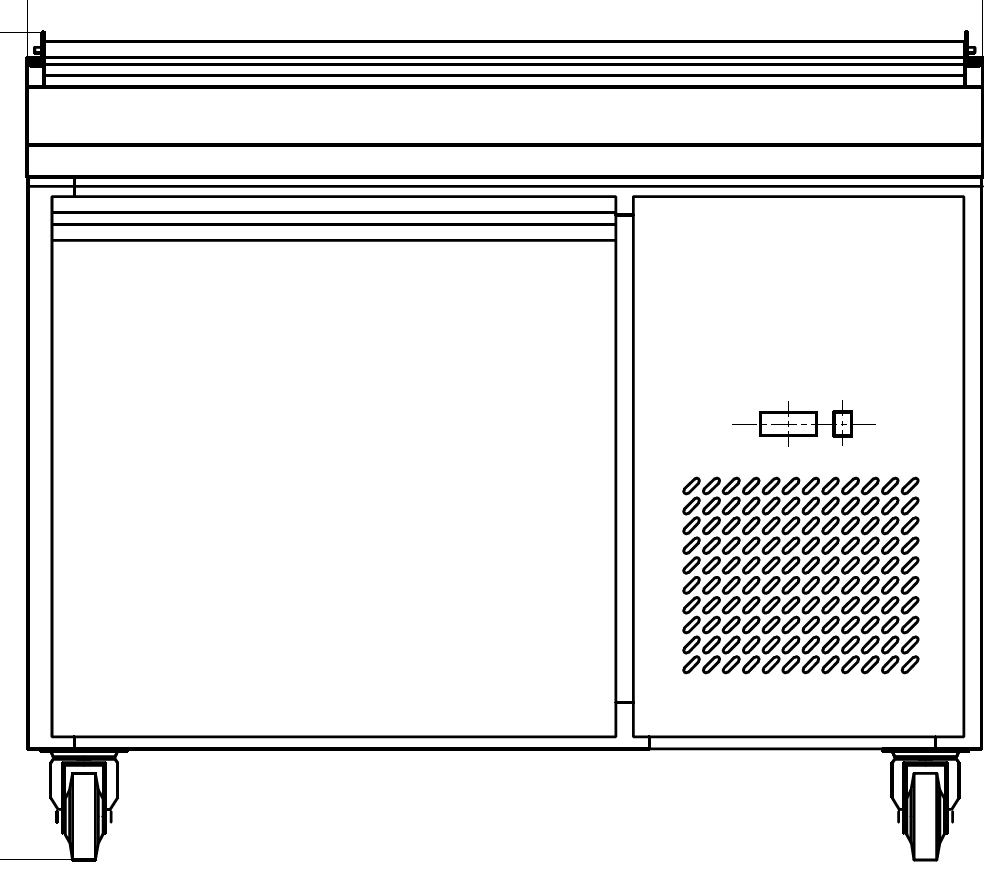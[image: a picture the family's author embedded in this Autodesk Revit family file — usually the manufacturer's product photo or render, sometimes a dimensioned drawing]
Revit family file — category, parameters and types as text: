
# Revit family: QF_Kelvinator_738252_KCHPT50.6
name_source: partatom
category: Specialty Equipment
units: mm (PartAtom-declared; Revit-internal decimal feet)

## family parameters
Always vertical = Yes
Cut with Voids When Loaded = No
Part Type = Normal
Room Calculation Point = No
Round Connector Dimension = Use Diameter
Shared = No
Work Plane-Based = No

## types (1)
- QF_Kelvinator_738252_KCHPT50.6
    Accessory = No
    Apparent Power = 0 VA
    Conn Conduit = Yes
    Conn Plug = 5-15P
    Cycle = 60 Hz
    Default Elevation = 0"
    Depth = 32 5/16"
    Depth Actual = 820"
    Description = 1-DOOR PIZZA PREP TABLE 48" LONG 6-1/3 PAN
    Elec Conn Connection Height = 0"
    Elec Conn RI Height = 0"
    FL Amps = 5 A
    Foodservice Equipment Identifier = Yes
    Gas KW = 0
    HP = 1 HP
    Height = 41 5/16"
    Height Actual = 1050"
    Identify Quantity as Lot = Yes
    Item Number = 738252
    Length = 47 3/8"
    Length Actual = 1203"
    Manufacturer = Kelvinator
    Max Overcurrent Protection = 0 A
    Min Ckt Ampacity = 0 A
    Model = KCHPT50.6
    Number of Poles = 1
    Phase = 1
    Refrigerant Type = R290
    URL = KELVINATOR
    URL Manufacturer = KELVINATOR
    Volts = 115 V
    Watts = 0 W
    Weight = 102.00 lbm
    Weight in Pounds = 224.872

## geometry (parser evidence)
native form markers: Sweep x9
no freeform markers — native parametric forms only
